# Revit family: SoapDispenser_Metlam_WallMounted_Vertical
name_source: partatom
category: Generic Models
revit_build: Autodesk Revit Architecture 2013 (Build: 20120221_2030(x64)
units: mm (PartAtom-declared; Revit-internal decimal feet)

## types (2) — shared parameters
Assembly Code = E1090900
Description = Horizontal Liquid Soap Dispenser Stainless Steel
FilterObject_ANZRS = Soap Dispenser
Height = 209 mm  [stored 0.685696 ft]
Keywords = CAPACITY 1.2L with lockable hinged lid (key provided)
Manufacturer = Metlam
Material Glass = Glass
Material Main = Stainless Steel, Satin
ModifiedIssue_ANZRS = 130318.01 $
StyleOrType_ANZRS = Sanitary Ware
URL = http://www.metlam.com.au
Width = 123 mm  [stored 0.403543 ft]

## per-type parameters (varying)
| type | Depth | Material Nozzle | Model | Nozzle ABS | Nozzle Standard | Product Code |
| Metlam WM Vertical Standard | 123 mm  [stored 0.403543 ft] | Stainless Steel, Polished | Wall Mounted Vertical Standard | No | Yes | ML 605 |
| Metlam WM Vertical ABS | 93 mm  [stored 0.305118 ft] | PC/ABS Plastic | Wall Mounted Vertical ABS | Yes | No | ML 605 BS |

note: [stored X ft] marks values corroborated as IEEE doubles in the binary element streams (Revit-internal decimal feet)

## geometry (parser evidence)
native form markers: Blend x11, Sweep x1
no freeform markers — native parametric forms only
